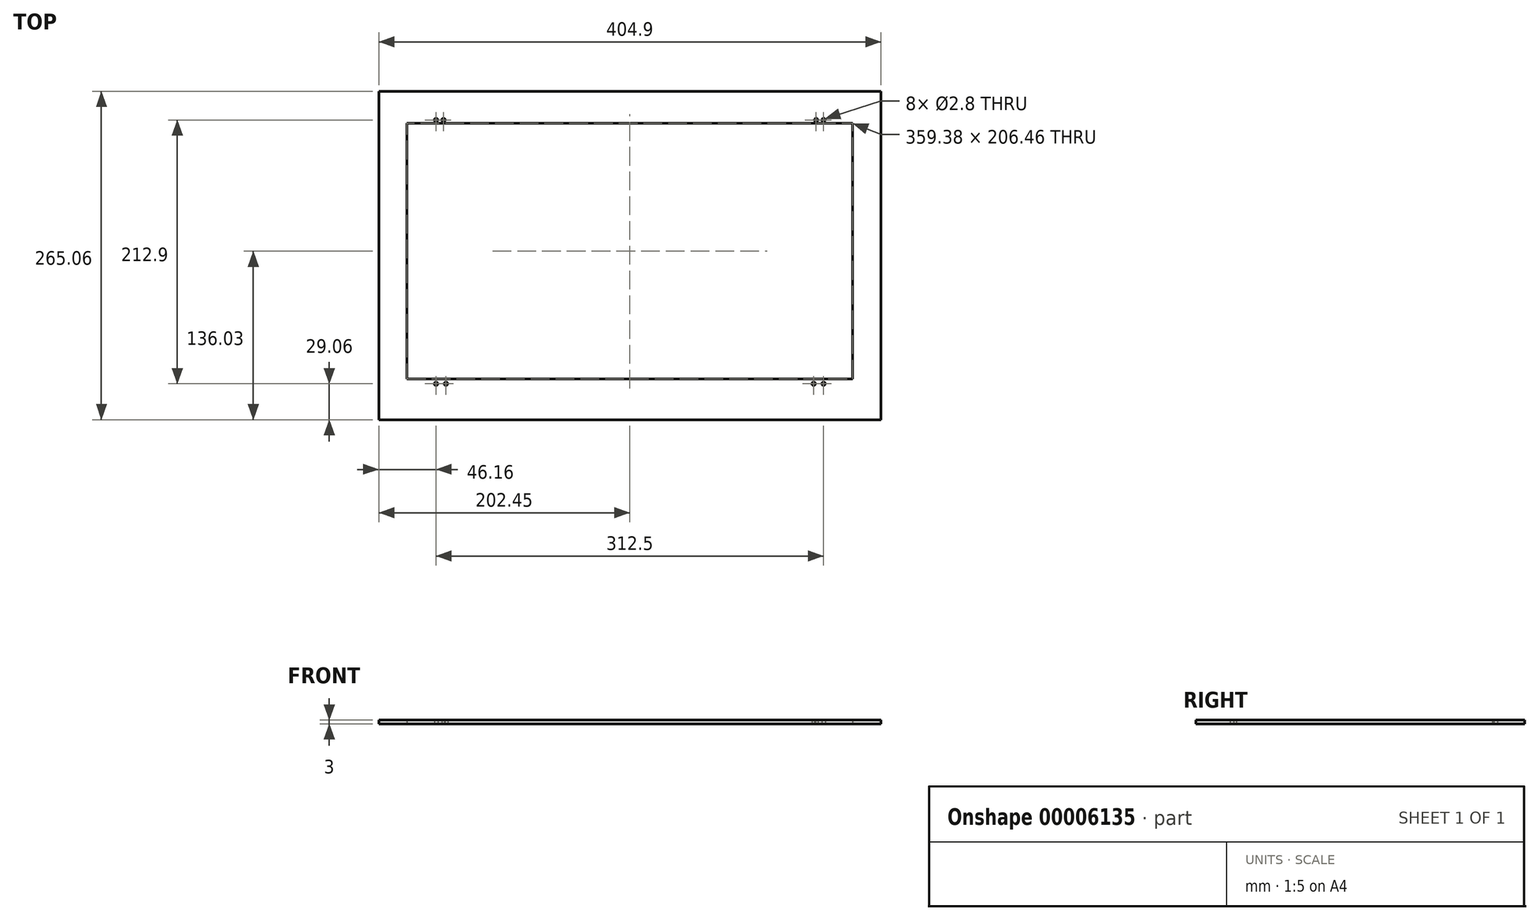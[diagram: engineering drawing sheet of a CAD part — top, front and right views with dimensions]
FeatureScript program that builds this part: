
annotation { "Feature Type Name" : "Feature", "Feature Type Description" : "" }
export const myFeature = defineFeature(function(context is Context, id is Id, definition is map)
    precondition{}
    {
        {
            var Q0;
            Q0=qCreatedBy(makeId("Top.planeOp"),FACE);
            var sketch = newSketch(context, id + "F0", { "sketchPlane" : qUnion([Q0])});
            skLineSegment(sketch, "E0", {"start": v(0, 0) * mm, "end": v(0, 107.57) * mm, "construction": true});
            skLineSegment(sketch, "E1", {"start": v(0, 0) * mm, "end": v(75.96, 0) * mm, "construction": true});
            skLineSegment(sketch, "E2", {"start": v(0, 107.57) * mm, "end": v(-182.45, 107.57) * mm, "construction": true});
            skLineSegment(sketch, "E3", {"start": v(-182.45, 107.57) * mm, "end": v(-182.45, -117.49) * mm, "construction": true});
            skLineSegment(sketch, "E4", {"start": v(-182.45, -117.49) * mm, "end": v(182.45, -117.49) * mm, "construction": true});
            skLineSegment(sketch, "E5.bottom", {"start": v(-182.45, -117.49) * mm, "end": v(182.45, -117.49) * mm});
            skLineSegment(sketch, "E5.top", {"start": v(-182.45, 107.57) * mm, "end": v(182.45, 107.57) * mm});
            skLineSegment(sketch, "E5.left", {"start": v(-182.45, -117.49) * mm, "end": v(-182.45, 107.57) * mm});
            skLineSegment(sketch, "E5.right", {"start": v(182.45, -117.49) * mm, "end": v(182.45, 107.57) * mm});
            skLineSegment(sketch, "E6.0", {"start": v(-202.45, 127.57) * mm, "end": v(202.45, 127.57) * mm});
            skLineSegment(sketch, "E6.1", {"start": v(-202.45, -137.49) * mm, "end": v(-202.45, 127.57) * mm});
            skLineSegment(sketch, "E6.2", {"start": v(-202.45, -137.49) * mm, "end": v(202.45, -137.49) * mm});
            skLineSegment(sketch, "E6.3", {"start": v(202.45, -137.49) * mm, "end": v(202.45, 127.57) * mm});
            skSolve(sketch);
        }
        {
            var Q0;
            Q0=makeQuery(id+"F0.imprint","IMPRINT",FACE,{"disambiguationData":[TD([[makeQuery(id+"F0.imprint","IMPRINT",EDGE,{"derivedFrom":sQuery(id+"F0.wireOp",EDGE,"E5.bottom")}),-1.0]])]});
            var Q1;
            Q1=makeQuery(id+"F0.imprint","IMPRINT",FACE,{"disambiguationData":[TD([[makeQuery(id+"F0.imprint","IMPRINT",EDGE,{"derivedFrom":sQuery(id+"F0.wireOp",EDGE,"E5.bottom")}),1.0]])]});
            extrude(context, id + "F1", {"entities" : qUnion([Q0, Q1]), "depth" : 3 * mm});
        }
        {
            var Q0;
            Q0=qCreatedBy(makeId("Top.planeOp"),FACE);
            var sketch = newSketch(context, id + "F2", { "sketchPlane" : qUnion([Q0])});
            skLineSegment(sketch, "E7", {"start": v(0, 0) * mm, "end": v(-182.45, 0) * mm, "construction": true});
            skLineSegment(sketch, "E8", {"start": v(-182.45, 0) * mm, "end": v(-182.45, 103.23) * mm, "construction": true});
            skLineSegment(sketch, "E9", {"start": v(-182.45, 103.23) * mm, "end": v(-156.3, 103.23) * mm, "construction": true});
            skLineSegment(sketch, "E10", {"start": v(-156.3, 103.23) * mm, "end": v(-156.3, 104.47) * mm, "construction": true});
            skLineSegment(sketch, "E11", {"start": v(-156.3, 104.47) * mm, "end": v(-150.3, 104.47) * mm, "construction": true});
            skCircle(sketch, "E12", {"center": v(-156.3, 104.47) * mm, "radius": 1.4 * mm});
            skCircle(sketch, "E13", {"center": v(-150.3, 104.47) * mm, "radius": 1.4 * mm});
            skLineSegment(sketch, "E14", {"start": v(-156.3, 104.47) * mm, "end": v(150.2, 104.47) * mm, "construction": true});
            skLineSegment(sketch, "E15", {"start": v(150.2, 104.47) * mm, "end": v(156.2, 104.47) * mm, "construction": true});
            skCircle(sketch, "E16", {"center": v(150.2, 104.47) * mm, "radius": 1.4 * mm});
            skCircle(sketch, "E17", {"center": v(156.2, 104.47) * mm, "radius": 1.4 * mm});
            skLineSegment(sketch, "E18", {"start": v(-156.3, 104.47) * mm, "end": v(-156.3, -108.43) * mm, "construction": true});
            skLineSegment(sketch, "E19", {"start": v(-156.3, -108.43) * mm, "end": v(-148.29, -108.43) * mm, "construction": true});
            skLineSegment(sketch, "E20", {"start": v(-156.3, -108.43) * mm, "end": v(148.2, -108.43) * mm, "construction": true});
            skLineSegment(sketch, "E21", {"start": v(148.2, -108.43) * mm, "end": v(156.2, -108.43) * mm});
            skCircle(sketch, "E22", {"center": v(156.2, -108.43) * mm, "radius": 1.4 * mm});
            skCircle(sketch, "E23", {"center": v(148.2, -108.43) * mm, "radius": 1.4 * mm});
            skCircle(sketch, "E24", {"center": v(-156.3, -108.43) * mm, "radius": 1.4 * mm});
            skCircle(sketch, "E25", {"center": v(-148.29, -108.43) * mm, "radius": 1.4 * mm});
            skSolve(sketch);
        }
        {
            var Q0;
            Q0=makeQuery(id+"F2.imprint","IMPRINT",FACE,{"disambiguationData":[TD([[makeQuery(id+"F2.imprint","IMPRINT",EDGE,{"derivedFrom":sQuery(id+"F2.wireOp",EDGE,"E12")}),1.0]])]});
            var Q1;
            Q1=makeQuery(id+"F2.imprint","IMPRINT",FACE,{"disambiguationData":[TD([[makeQuery(id+"F2.imprint","IMPRINT",EDGE,{"derivedFrom":sQuery(id+"F2.wireOp",EDGE,"E13")}),1.0]])]});
            var Q2;
            Q2=makeQuery(id+"F2.imprint","IMPRINT",FACE,{"disambiguationData":[TD([[makeQuery(id+"F2.imprint","IMPRINT",EDGE,{"derivedFrom":sQuery(id+"F2.wireOp",EDGE,"E16")}),1.0]])]});
            var Q3;
            Q3=makeQuery(id+"F2.imprint","IMPRINT",FACE,{"disambiguationData":[TD([[makeQuery(id+"F2.imprint","IMPRINT",EDGE,{"derivedFrom":sQuery(id+"F2.wireOp",EDGE,"E17")}),1.0]])]});
            var Q4;
            Q4=makeQuery(id+"F2.imprint","IMPRINT",FACE,{"disambiguationData":[TD([[makeQuery(id+"F2.imprint","IMPRINT",EDGE,{"derivedFrom":sQuery(id+"F2.wireOp",EDGE,"E24")}),1.0]])]});
            var Q5;
            Q5=makeQuery(id+"F2.imprint","IMPRINT",FACE,{"disambiguationData":[TD([[makeQuery(id+"F2.imprint","IMPRINT",EDGE,{"derivedFrom":sQuery(id+"F2.wireOp",EDGE,"E25")}),1.0]])]});
            var Q6;
            Q6=makeQuery(id+"F2.imprint","IMPRINT",FACE,{"disambiguationData":[TD([[makeQuery(id+"F2.imprint","IMPRINT",EDGE,{"derivedFrom":sQuery(id+"F2.wireOp",EDGE,"E23")}),1.0]])]});
            var Q7;
            Q7=makeQuery(id+"F2.imprint","IMPRINT",FACE,{"disambiguationData":[TD([[makeQuery(id+"F2.imprint","IMPRINT",EDGE,{"derivedFrom":sQuery(id+"F2.wireOp",EDGE,"E22")}),1.0]])]});
            extrude(context, id + "F3", {"entities" : qUnion([Q0, Q1, Q2, Q3, Q4, Q5, Q6, Q7]), "operationType" : NewBodyOperationType.REMOVE, "depth" : 3 * mm});
        }
        {
            var Q0;
            Q0=qCreatedBy(makeId("Top.planeOp"),FACE);
            var sketch = newSketch(context, id + "F4", { "sketchPlane" : qUnion([Q0])});
            skLineSegment(sketch, "E26.rect.bottom", {"start": v(179.7, 101.77) * mm, "end": v(-179.69, 101.77) * mm});
            skLineSegment(sketch, "E26.rect.top", {"start": v(179.69, -104.69) * mm, "end": v(-179.7, -104.69) * mm});
            skLineSegment(sketch, "E26.rect.left", {"start": v(179.7, 101.77) * mm, "end": v(179.69, -104.7) * mm});
            skLineSegment(sketch, "E26.rect.right", {"start": v(-179.69, 101.77) * mm, "end": v(-179.7, -104.69) * mm});
            skPoint(sketch, "E26.rect.middle", {"position": v(0, -1.46) * mm});
            skSolve(sketch);
        }
        {
            var Q0;
            Q0=makeQuery(id+"F4.imprint","IMPRINT",FACE,{"disambiguationData":[TD([[makeQuery(id+"F4.imprint","IMPRINT",EDGE,{"derivedFrom":sQuery(id+"F4.wireOp",EDGE,"E26.rect.bottom")}),1.0]])]});
            extrude(context, id + "F5", {"entities" : qUnion([Q0]), "operationType" : NewBodyOperationType.REMOVE, "endBound" : BoundingType.UP_TO_NEXT, "depth" : 25 * mm});
        }
    });
